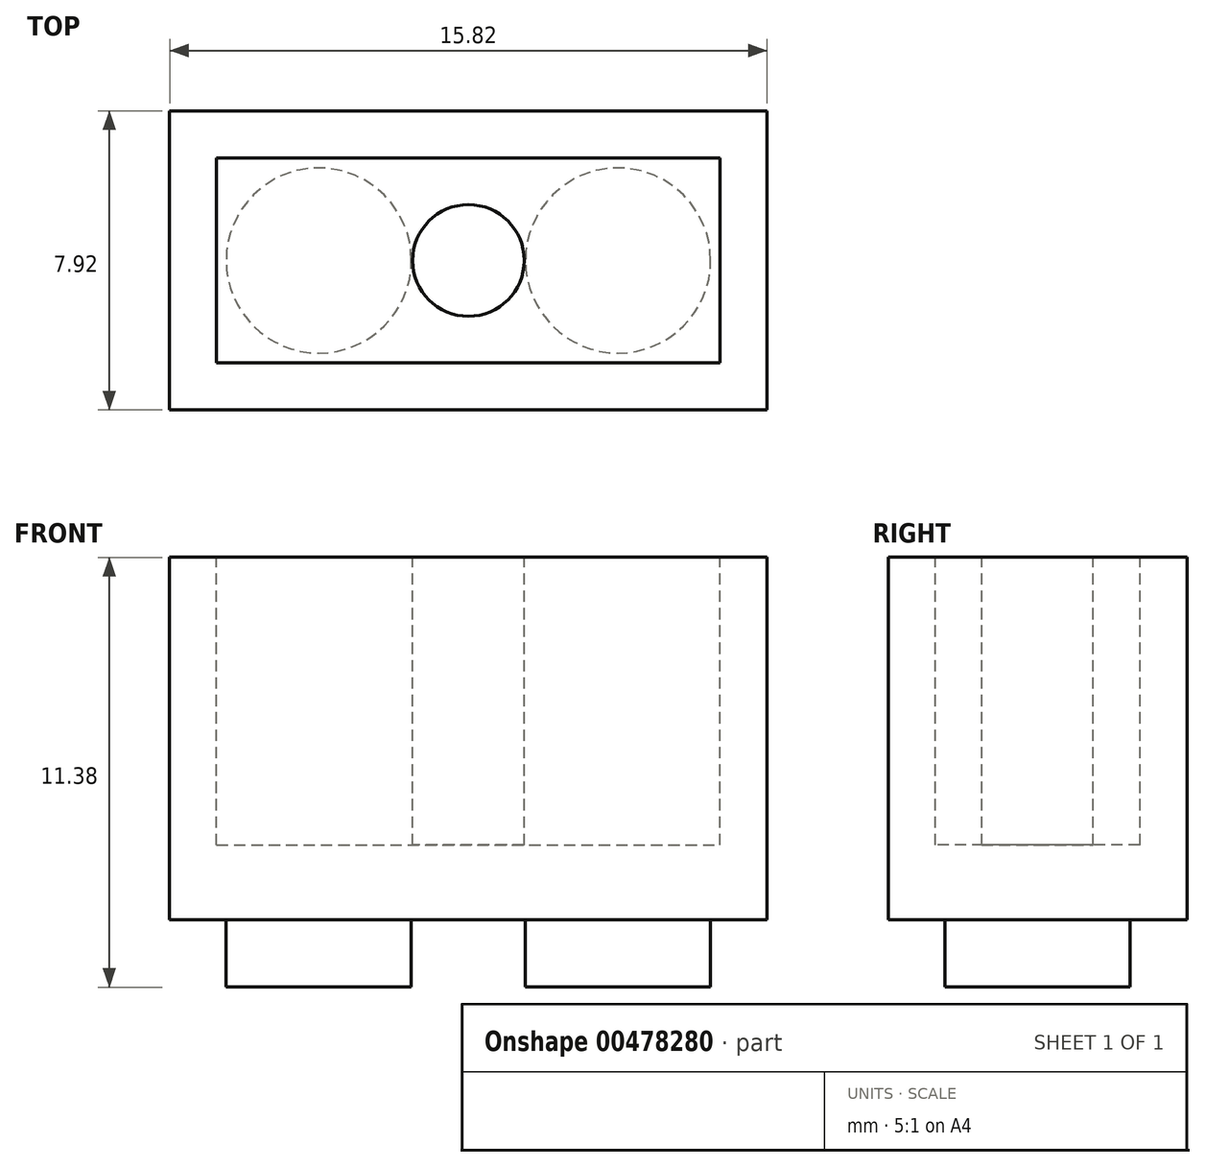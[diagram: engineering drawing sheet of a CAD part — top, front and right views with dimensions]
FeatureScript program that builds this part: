
annotation { "Feature Type Name" : "Feature", "Feature Type Description" : "" }
export const myFeature = defineFeature(function(context is Context, id is Id, definition is map)
    precondition{}
    {
        {
            var Q0;
            Q0=qCreatedBy(makeId("Top.planeOp"),FACE);
            var sketch = newSketch(context, id + "F0", { "sketchPlane" : qUnion([Q0])});
            skLineSegment(sketch, "E0.bottom", {"start": v(-7.91, 3.96) * mm, "end": v(7.91, 3.96) * mm});
            skLineSegment(sketch, "E0.top", {"start": v(-7.91, -3.96) * mm, "end": v(7.91, -3.96) * mm});
            skLineSegment(sketch, "E0.left", {"start": v(-7.91, 3.96) * mm, "end": v(-7.91, -3.96) * mm});
            skLineSegment(sketch, "E0.right", {"start": v(7.91, 3.96) * mm, "end": v(7.91, -3.96) * mm});
            skPoint(sketch, "E0.middle", {"position": v(0, 0) * mm});
            skSolve(sketch);
        }
        {
            var Q0;
            Q0=makeQuery(id+"F0.imprint","IMPRINT",FACE,{"disambiguationData":[TD([[makeQuery(id+"F0.imprint","IMPRINT",EDGE,{"derivedFrom":sQuery(id+"F0.wireOp",EDGE,"E0.bottom")}),-1.0]])]});
            var sketch = newSketch(context, id + "F1", { "sketchPlane" : qUnion([Q0])});
            skCircle(sketch, "E1", {"center": v(-3.96, 0) * mm, "radius": 2.45 * mm});
            skCircle(sketch, "E2", {"center": v(3.96, 0) * mm, "radius": 2.45 * mm});
            skSolve(sketch);
        }
        {
            var Q0;
            Q0=makeQuery(id+"F0.imprint","IMPRINT",FACE,{"disambiguationData":[TD([[makeQuery(id+"F0.imprint","IMPRINT",EDGE,{"derivedFrom":sQuery(id+"F0.wireOp",EDGE,"E0.bottom")}),-1.0]])]});
            extrude(context, id + "F2", {"entities" : qUnion([Q0]), "depth" : 9.6 * mm, "offsetDistance" : 25.4 * mm});
        }
        {
            var Q0;
            Q0=makeQuery(id+"F1.imprint","IMPRINT",FACE,{"disambiguationData":[TD([[makeQuery(id+"F1.imprint","IMPRINT",EDGE,{"derivedFrom":sQuery(id+"F1.wireOp",EDGE,"E1")}),1.0]])]});
            var Q1;
            Q1=makeQuery(id+"F1.imprint","IMPRINT",FACE,{"disambiguationData":[TD([[makeQuery(id+"F1.imprint","IMPRINT",EDGE,{"derivedFrom":sQuery(id+"F1.wireOp",EDGE,"E2")}),1.0]])]});
            extrude(context, id + "F3", {"entities" : qUnion([Q0, Q1]), "operationType" : NewBodyOperationType.ADD, "oppositeDirection" : true, "depth" : 1.78 * mm, "offsetDistance" : 25.4 * mm});
        }
        {
            var Q0;
            Q0=makeQuery(id+"F2.opExtrude","CAP_FACE",FACE,{"disambiguationData":[OSD([sQuery(id+"F0.wireOp",EDGE,"E0.bottom"),sQuery(id+"F0.wireOp",EDGE,"E0.top"),sQuery(id+"F0.wireOp",EDGE,"E0.left"),sQuery(id+"F0.wireOp",EDGE,"E0.right")])],"isStart":false});
            var sketch = newSketch(context, id + "F4", { "sketchPlane" : qUnion([Q0])});
            skPoint(sketch, "E3.middle", {"position": v(0, 0) * mm});
            skLineSegment(sketch, "E4.bottom", {"start": v(-6.67, 2.71) * mm, "end": v(6.67, 2.71) * mm});
            skLineSegment(sketch, "E4.top", {"start": v(-6.67, -2.71) * mm, "end": v(6.67, -2.71) * mm});
            skLineSegment(sketch, "E4.left", {"start": v(-6.67, 2.71) * mm, "end": v(-6.67, -2.71) * mm});
            skLineSegment(sketch, "E4.right", {"start": v(6.67, 2.71) * mm, "end": v(6.67, -2.71) * mm});
            skSolve(sketch);
        }
        {
            var Q0;
            Q0=makeQuery(id+"F4.imprint","IMPRINT",FACE,{"disambiguationData":[TD([[makeQuery(id+"F4.imprint","IMPRINT",EDGE,{"derivedFrom":sQuery(id+"F4.wireOp",EDGE,"E4.bottom")}),-1.0]])]});
            var sketch = newSketch(context, id + "F5", { "sketchPlane" : qUnion([Q0])});
            skCircle(sketch, "E5", {"center": v(0, 0) * mm, "radius": 1.48 * mm});
            skSolve(sketch);
        }
        {
            var Q0;
            Q0=makeQuery(id+"F4.imprint","IMPRINT",FACE,{"disambiguationData":[TD([[makeQuery(id+"F4.imprint","IMPRINT",EDGE,{"derivedFrom":sQuery(id+"F4.wireOp",EDGE,"E4.bottom")}),-1.0]])]});
            extrude(context, id + "F6", {"entities" : qUnion([Q0]), "operationType" : NewBodyOperationType.REMOVE, "oppositeDirection" : true, "depth" : 7.62 * mm, "offsetDistance" : 25.4 * mm});
        }
        {
            var Q0;
            Q0=makeQuery(id+"F5.imprint","IMPRINT",FACE,{"disambiguationData":[TD([[makeQuery(id+"F5.imprint","IMPRINT",EDGE,{"derivedFrom":sQuery(id+"F5.wireOp",EDGE,"E5")}),1.0]])]});
            extrude(context, id + "F7", {"entities" : qUnion([Q0]), "operationType" : NewBodyOperationType.ADD, "oppositeDirection" : true, "depth" : 8.13 * mm, "offsetDistance" : 25.4 * mm});
        }
    });
